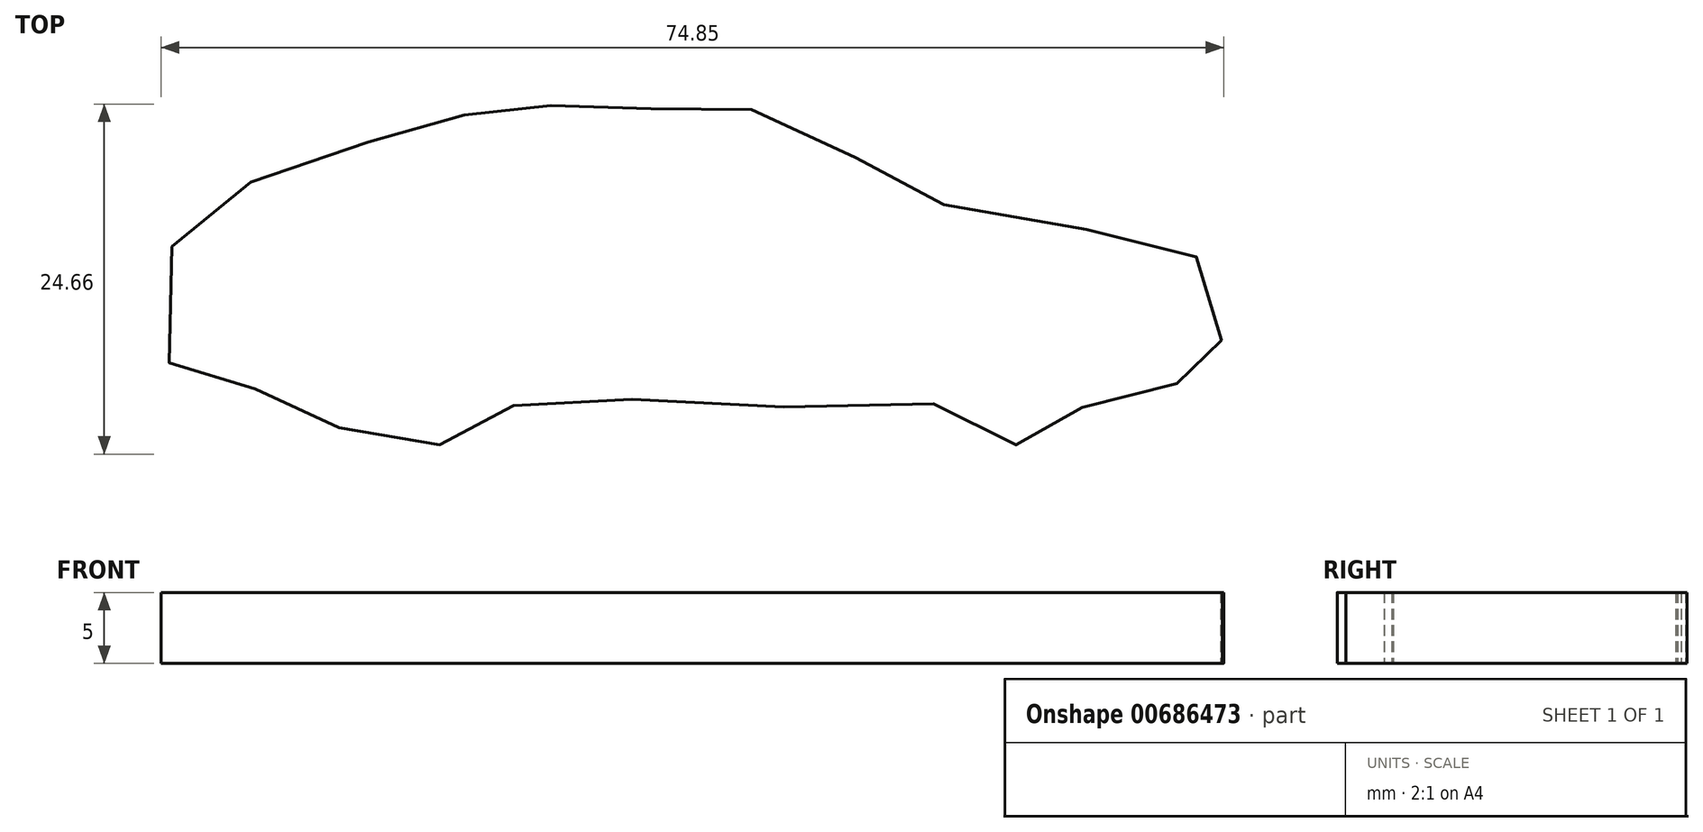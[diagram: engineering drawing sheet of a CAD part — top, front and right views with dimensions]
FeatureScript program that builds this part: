
annotation { "Feature Type Name" : "Feature", "Feature Type Description" : "" }
export const myFeature = defineFeature(function(context is Context, id is Id, definition is map)
    precondition{}
    {
        {
            var Q0;
            Q0=qCreatedBy(makeId("Top.planeOp"),FACE);
            var sketch = newSketch(context, id + "F0", { "sketchPlane" : qUnion([Q0])});
            skFitSpline(sketch, "E0", {"points": [v(-20.22, 9.96) * mm, v(-17.88, 8.2) * mm, v(-13.38, 7.03) * mm, v(-10.65, 8.2) * mm, v(-9.48, 9.96) * mm, v(-5.18, 10.94) * mm, v(-1.66, 11.72) * mm, v(0, 12.5) * mm, v(0, 15.44) * mm, v(0, 18.56) * mm, v(-4.6, 21.69) * mm, v(-9.87, 22.27) * mm, v(-19.05, 23.84) * mm, v(-22.37, 25.4) * mm, v(-27.26, 28.14) * mm, v(-32.34, 30.48) * mm, v(-36.63, 31.07) * mm, v(-41.13, 30.68) * mm, v(-45.62, 30.87) * mm, v(-48.94, 30.87) * mm, v(-52.07, 30.28) * mm, v(-56.17, 30.28) * mm, v(-60.47, 28.14) * mm, v(-66.72, 25.8) * mm, v(-72.39, 24.42) * mm, v(-74.25, 18.56) * mm, v(-74.25, 13.1) * mm, v(-71.41, 11.53) * mm, v(-67.5, 10.94) * mm, v(-62.82, 9.77) * mm, v(-61.45, 7.23) * mm, v(-55.59, 6.84) * mm, v(-52.07, 8.99) * mm, v(-49.92, 9.77) * mm, v(-48.94, 10.16) * mm, v(-39.17, 10.16) * mm, v(-29.8, 9.77) * mm, v(-20.22, 9.96) * mm]});
            skSolve(sketch);
        }
        {
            var Q0;
            Q0 = qSketchRegion(id + "F0", true);
            extrude(context, id + "F1", {"entities" : qUnion([Q0]), "depth" : 5 * mm, "offsetDistance" : 25.4 * mm});
        }
    });
